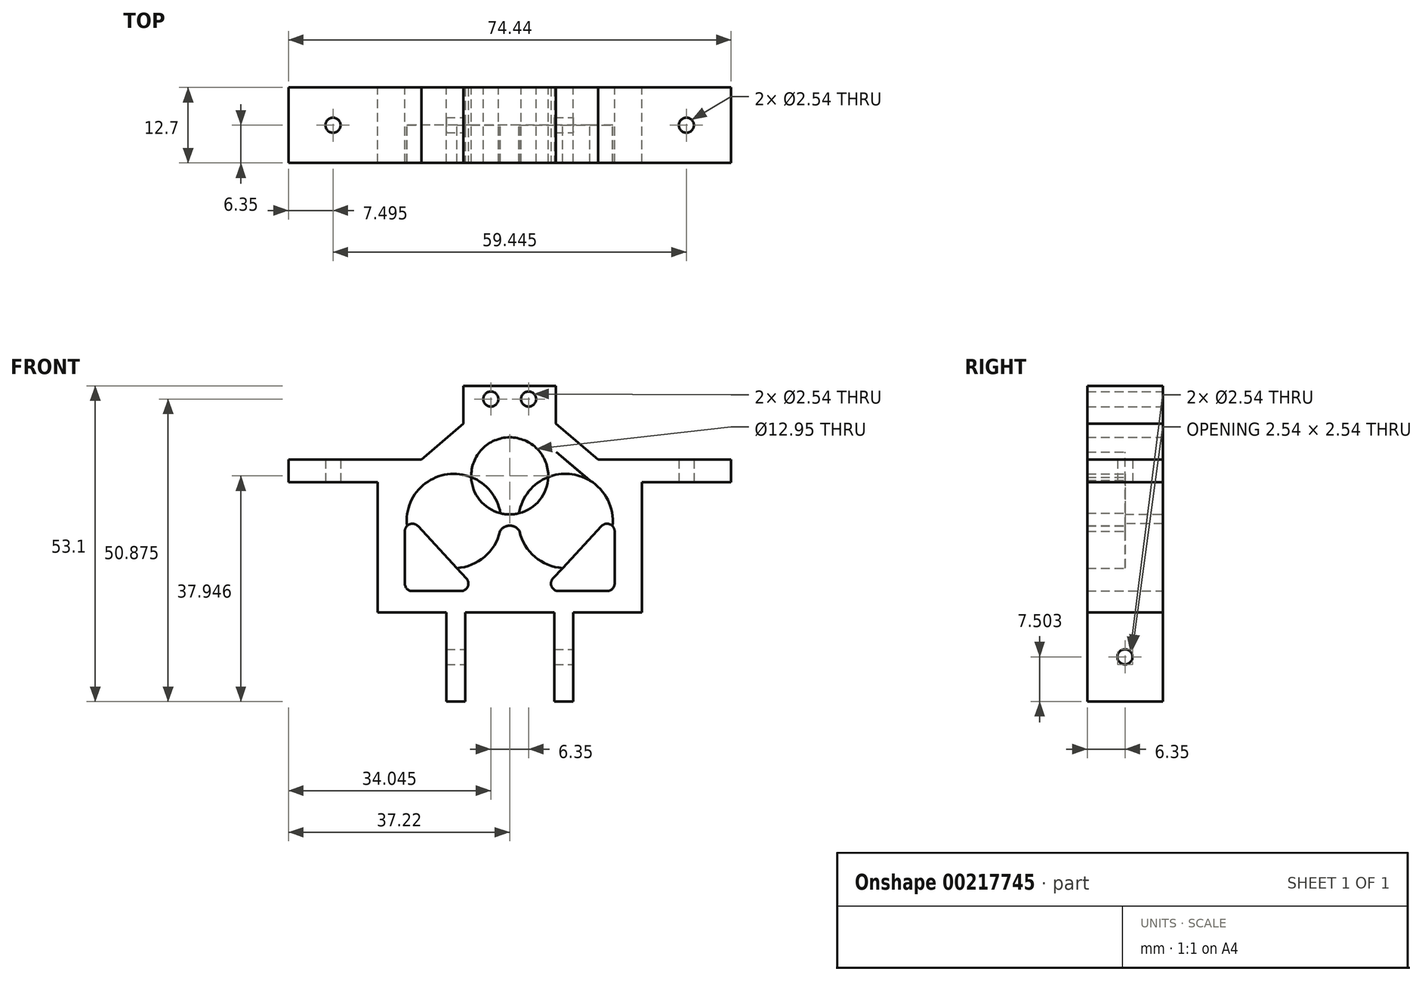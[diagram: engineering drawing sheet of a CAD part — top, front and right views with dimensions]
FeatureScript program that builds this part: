
annotation { "Feature Type Name" : "Feature", "Feature Type Description" : "" }
export const myFeature = defineFeature(function(context is Context, id is Id, definition is map)
    precondition{}
    {
        {
            var Q0;
            Q0=qCreatedBy(makeId("Front.planeOp"),FACE);
            var sketch = newSketch(context, id + "F0", { "sketchPlane" : qUnion([Q0])});
            skLineSegment(sketch, "E0", {"start": v(0, 0.13) * mm, "end": v(7.5, 0.13) * mm});
            skLineSegment(sketch, "E1", {"start": v(-22.22, 19.5) * mm, "end": v(-22.22, 4.52) * mm});
            skLineSegment(sketch, "E2", {"start": v(-7.5, 0.13) * mm, "end": v(0, 0.13) * mm});
            skArc(sketch, "E3", {"start": v(-13.47, 22.3) * mm, "mid": v(-14.04, 9.06) * mm, "end": v(-1.65, 13.77) * mm});
            skArc(sketch, "E4.MirrorC", {"start": v(13.47, 22.3) * mm, "mid": v(14.05, 9.06) * mm, "end": v(1.65, 13.75) * mm});
            skArc(sketch, "E5", {"start": v(1.65, 13.75) * mm, "mid": v(0, 14.71) * mm, "end": v(-1.65, 13.77) * mm});
            skLineSegment(sketch, "E6", {"start": v(-22.22, 19.5) * mm, "end": v(-22.22, 0.13) * mm});
            skLineSegment(sketch, "E7.MirrorCS", {"start": v(22.22, 19.5) * mm, "end": v(22.22, 0.13) * mm});
            skLineSegment(sketch, "E8", {"start": v(0, 0.13) * mm, "end": v(-22.22, 0.13) * mm});
            skLineSegment(sketch, "E9", {"start": v(0, 0.13) * mm, "end": v(22.22, 0.13) * mm});
            skPoint(sketch, "E10.orphan", {"position": v(-22.22, 0) * mm});
            skLineSegment(sketch, "E11", {"start": v(-3.18, 27.12) * mm, "end": v(-3.18, 30.3) * mm});
            skLineSegment(sketch, "E12", {"start": v(3.17, 30.3) * mm, "end": v(3.17, 27.12) * mm});
            skLineSegment(sketch, "E13", {"start": v(3.17, 27.12) * mm, "end": v(3.17, 27.12) * mm});
            skLineSegment(sketch, "E14", {"start": v(-22.22, 19.5) * mm, "end": v(-7.77, 31.88) * mm});
            skLineSegment(sketch, "E15", {"start": v(-3.18, 27.12) * mm, "end": v(-7.84, 27.12) * mm});
            skLineSegment(sketch, "E16", {"start": v(-13.47, 22.3) * mm, "end": v(-7.84, 27.12) * mm});
            skLineSegment(sketch, "E17.MirrorCS", {"start": v(3.17, 27.12) * mm, "end": v(7.84, 27.12) * mm});
            skLineSegment(sketch, "E18.MirrorCS", {"start": v(13.46, 22.3) * mm, "end": v(7.84, 27.12) * mm});
            skLineSegment(sketch, "E19.MirrorCS", {"start": v(3.17, 30.3) * mm, "end": v(3.18, 30.3) * mm});
            skLineSegment(sketch, "E20.MirrorCS", {"start": v(22.22, 19.5) * mm, "end": v(7.77, 31.88) * mm});
            skPoint(sketch, "E21.end.orphan", {"position": v(-9.63, 30.3) * mm});
            skPoint(sketch, "E22.orphan", {"position": v(9.62, 30.3) * mm});
            skPoint(sketch, "E23.start.orphan", {"position": v(0, 27.12) * mm});
            skLineSegment(sketch, "E24", {"start": v(13.47, 22.3) * mm, "end": v(7.84, 27.12) * mm});
            skLineSegment(sketch, "E25", {"start": v(3.17, 27.12) * mm, "end": v(3.17, 30.3) * mm});
            skLineSegment(sketch, "E26", {"start": v(-3.18, 30.3) * mm, "end": v(-3.18, 27.12) * mm});
            skLineSegment(sketch, "E27", {"start": v(-7.84, 27.12) * mm, "end": v(-13.47, 22.3) * mm});
            skArc(sketch, "E28", {"start": v(1.65, 13.75) * mm, "mid": v(14.06, 9.07) * mm, "end": v(13.45, 22.31) * mm});
            skPoint(sketch, "E29.startSnap0", {"position": v(0, 30.3) * mm});
            skPoint(sketch, "E30.orphan", {"position": v(22.22, 2.54) * mm});
            skLineSegment(sketch, "E31", {"start": v(3.17, 30.3) * mm, "end": v(3.17, 33.47) * mm});
            skLineSegment(sketch, "E32", {"start": v(3.17, 33.47) * mm, "end": v(-3.18, 33.47) * mm});
            skLineSegment(sketch, "E33", {"start": v(-3.18, 33.47) * mm, "end": v(-3.18, 30.3) * mm});
            skLineSegment(sketch, "E34", {"start": v(-7.77, 31.88) * mm, "end": v(-7.77, 38.23) * mm});
            skLineSegment(sketch, "E35", {"start": v(7.77, 31.88) * mm, "end": v(7.77, 38.23) * mm});
            skLineSegment(sketch, "E36", {"start": v(7.77, 38.23) * mm, "end": v(-7.77, 38.23) * mm});
            skCircle(sketch, "E37", {"center": v(-9.4, 15.5) * mm, "radius": 7.94 * mm});
            skCircle(sketch, "E38", {"center": v(9.4, 15.5) * mm, "radius": 7.94 * mm});
            skCircle(sketch, "E39", {"center": v(0, 23.08) * mm, "radius": 6.48 * mm});
            skLineSegment(sketch, "E40", {"start": v(-22.22, 0.13) * mm, "end": v(-22.22, 25.81) * mm});
            skLineSegment(sketch, "E41", {"start": v(-22.22, 25.81) * mm, "end": v(-17.42, 25.81) * mm});
            skLineSegment(sketch, "E42", {"start": v(-17.42, 25.81) * mm, "end": v(-12.1, 25.81) * mm});
            skLineSegment(sketch, "E43", {"start": v(0, 12.81) * mm, "end": v(0, 7.67) * mm});
            skLineSegment(sketch, "E44.MirrorCS", {"start": v(22.22, 0.13) * mm, "end": v(22.22, 25.81) * mm});
            skLineSegment(sketch, "E45.MirrorCS", {"start": v(22.22, 25.81) * mm, "end": v(17.42, 25.81) * mm});
            skLineSegment(sketch, "E46.MirrorCS", {"start": v(17.42, 25.81) * mm, "end": v(12.09, 25.81) * mm});
            skCircle(sketch, "E47", {"center": v(3.17, 36) * mm, "radius": 1.27 * mm});
            skCircle(sketch, "E48", {"center": v(-3.18, 36) * mm, "radius": 1.27 * mm});
            skSolve(sketch);
        }
        {
            var Q0;
            Q0=qSketchRegion(id+"F0",true);
            var Q1;
            {var subQ0=sQuery(id+"F0.wireOp",EDGE,"E38");var subQ1=makeQuery(id+"F0.imprint","INTERSECT",VERTEX,{"derivedFrom":[sQuery(id+"F0.wireOp",EDGE,"E24"),subQ0]});Q1=makeQuery(id+"F0.imprint","IMPRINT",FACE,{"disambiguationData":[TD([[makeQuery(id+"F0.imprint","IMPRINT",EDGE,{"disambiguationData":[TD([[subQ1,-1.0]])],"derivedFrom":subQ0}),1.0]])]});}
            var Q2;
            {var subQ0=sQuery(id+"F0.wireOp",EDGE,"E37");var subQ1=makeQuery(id+"F0.imprint","INTERSECT",VERTEX,{"derivedFrom":[sQuery(id+"F0.wireOp",EDGE,"E27"),subQ0]});Q2=makeQuery(id+"F0.imprint","IMPRINT",FACE,{"disambiguationData":[TD([[makeQuery(id+"F0.imprint","IMPRINT",EDGE,{"disambiguationData":[TD([[subQ1,-1.0]])],"derivedFrom":subQ0}),1.0]])]});}
            var Q3;
            Q3=makeQuery(id+"F0.imprint","IMPRINT",FACE,{"disambiguationData":[TD([[makeQuery(id+"F0.imprint","IMPRINT",EDGE,{"derivedFrom":sQuery(id+"F0.wireOp",EDGE,"E15")}),1.0]])]});
            var Q4;
            {var subQ4=sQuery(id+"F0.wireOp",EDGE,"E31");Q4=makeQuery(id+"F0.imprint","IMPRINT",FACE,{"disambiguationData":[TD([[makeQuery(id+"F0.imprint","IMPRINT",EDGE,{"derivedFrom":subQ4}),1.0]])]});}
            var Q5;
            {var subQ0=sQuery(id+"F0.wireOp",EDGE,"E18.MirrorCS");var subQ5=sQuery(id+"F0.wireOp",EDGE,"E38");var subQ6=makeQuery(id+"F0.imprint","INTERSECT",VERTEX,{"derivedFrom":[subQ0,subQ5]});Q5=makeQuery(id+"F0.imprint","IMPRINT",FACE,{"disambiguationData":[TD([[makeQuery(id+"F0.imprint","IMPRINT",EDGE,{"disambiguationData":[TD([[subQ6,-1.0]])],"derivedFrom":subQ5}),-1.0]])]});}
            var Q6;
            {var subQ0=sQuery(id+"F0.wireOp",EDGE,"E5");Q6=makeQuery(id+"F0.imprint","IMPRINT",FACE,{"disambiguationData":[TD([[makeQuery(id+"F0.imprint","IMPRINT",EDGE,{"derivedFrom":subQ0}),-1.0]])]});}
            extrude(context, id + "F1", {"entities" : qUnion([Q0, Q1, Q2, Q3, Q4, Q5, Q6]), "depth" : 6.35 * mm, "offsetDistance" : 25.4 * mm});
        }
        {
            var Q0;
            Q0=makeQuery(id+"F1.opExtrude","CAP_FACE",FACE,{"disambiguationData":[OSD([sQuery(id+"F0.wireOp",EDGE,"E6"),sQuery(id+"F0.wireOp",EDGE,"E7.MirrorCS"),sQuery(id+"F0.wireOp",EDGE,"E8"),sQuery(id+"F0.wireOp",EDGE,"E9"),sQuery(id+"F0.wireOp",EDGE,"E14"),sQuery(id+"F0.wireOp",EDGE,"E18.MirrorCS"),sQuery(id+"F0.wireOp",EDGE,"E20.MirrorCS"),sQuery(id+"F0.wireOp",EDGE,"E24"),sQuery(id+"F0.wireOp",EDGE,"E34"),sQuery(id+"F0.wireOp",EDGE,"E35"),sQuery(id+"F0.wireOp",EDGE,"E36"),sQuery(id+"F0.wireOp",EDGE,"E38"),sQuery(id+"F0.wireOp",EDGE,"E39")])],"isStart":true});
            var sketch = newSketch(context, id + "F2", { "sketchPlane" : qUnion([Q0])});
            skCircle(sketch, "E49", {"center": v(0, 23.08) * mm, "radius": 6.48 * mm});
            skLineSegment(sketch, "E50", {"start": v(-22.22, 0.13) * mm, "end": v(22.22, 0.13) * mm});
            skLineSegment(sketch, "E51", {"start": v(7.77, 31.88) * mm, "end": v(7.77, 31.88) * mm});
            skLineSegment(sketch, "E52", {"start": v(7.77, 31.88) * mm, "end": v(7.77, 38.23) * mm});
            skLineSegment(sketch, "E53", {"start": v(7.77, 38.23) * mm, "end": v(-7.77, 38.23) * mm});
            skLineSegment(sketch, "E54", {"start": v(-7.77, 38.23) * mm, "end": v(-7.77, 31.88) * mm});
            skLineSegment(sketch, "E55", {"start": v(-7.77, 31.88) * mm, "end": v(-7.77, 31.88) * mm});
            skLineSegment(sketch, "E56", {"start": v(22.22, 0.13) * mm, "end": v(22.22, 25.81) * mm});
            skLineSegment(sketch, "E57", {"start": v(-22.22, 0.13) * mm, "end": v(-22.22, 25.81) * mm});
            skLineSegment(sketch, "E58", {"start": v(-22.22, 25.81) * mm, "end": v(-14.86, 25.81) * mm});
            skLineSegment(sketch, "E59", {"start": v(-14.86, 25.81) * mm, "end": v(-7.77, 31.88) * mm});
            skLineSegment(sketch, "E60", {"start": v(22.22, 25.81) * mm, "end": v(14.86, 25.81) * mm});
            skLineSegment(sketch, "E61", {"start": v(14.86, 25.81) * mm, "end": v(7.77, 31.88) * mm});
            skCircle(sketch, "E62", {"center": v(-3.17, 36) * mm, "radius": 1.27 * mm});
            skCircle(sketch, "E63", {"center": v(3.18, 36) * mm, "radius": 1.27 * mm});
            skSolve(sketch);
        }
        {
            var Q0;
            Q0=qSketchRegion(id+"F2",true);
            extrude(context, id + "F3", {"entities" : qUnion([Q0]), "operationType" : NewBodyOperationType.ADD, "depth" : 6.35 * mm});
        }
        {
            var Q0;
            Q0=makeQuery(id+"F3.boolean.opBoolean","MERGE",FACE,{"derivedFrom":[makeQuery(id+"F1.opExtrude","SWEPT_FACE",FACE,{"disambiguationData":[OSD([sQuery(id+"F0.wireOp",EDGE,"E40")])]}),makeQuery(id+"F3.opExtrude","SWEPT_FACE",FACE,{"disambiguationData":[OSD([sQuery(id+"F2.wireOp",EDGE,"E56")])]})]});
            var sketch = newSketch(context, id + "F4", { "sketchPlane" : qUnion([Q0])});
            skLineSegment(sketch, "E64", {"start": v(6.35, 0.13) * mm, "end": v(6.35, 22) * mm});
            skLineSegment(sketch, "E65", {"start": v(6.35, 22) * mm, "end": v(-6.35, 22) * mm});
            skLineSegment(sketch, "E66", {"start": v(-6.35, 22) * mm, "end": v(-6.35, 25.81) * mm});
            skLineSegment(sketch, "E67", {"start": v(-6.35, 25.81) * mm, "end": v(6.35, 25.81) * mm});
            skLineSegment(sketch, "E68", {"start": v(6.35, 25.81) * mm, "end": v(6.35, 22) * mm});
            skSolve(sketch);
        }
        {
            var Q0;
            Q0=qSketchRegion(id+"F4",true);
            extrude(context, id + "F5", {"entities" : qUnion([Q0]), "operationType" : NewBodyOperationType.ADD, "depth" : 15 * mm});
        }
        {
            var Q0;
            Q0=makeQuery(id+"F5.opExtrude","SWEPT_FACE",FACE,{"disambiguationData":[OSD([sQuery(id+"F4.wireOp",EDGE,"E65")])]});
            var sketch = newSketch(context, id + "F6", { "sketchPlane" : qUnion([Q0])});
            skLineSegment(sketch, "E69", {"start": v(-37.22, -6.35) * mm, "end": v(-22.22, 6.35) * mm});
            skCircle(sketch, "E70", {"center": v(-29.72, 0) * mm, "radius": 1.27 * mm});
            skSolve(sketch);
        }
        {
            var Q0;
            Q0=qSketchRegion(id+"F6",true);
            extrude(context, id + "F7", {"entities" : qUnion([Q0]), "operationType" : NewBodyOperationType.REMOVE, "oppositeDirection" : true, "depth" : 25.4 * mm});
        }
        {
            var Q0;
            Q0=makeQuery(id+"F3.boolean.opBoolean","MERGE",FACE,{"derivedFrom":[makeQuery(id+"F1.opExtrude","SWEPT_FACE",FACE,{"disambiguationData":[OSD([sQuery(id+"F0.wireOp",EDGE,"E44.MirrorCS")])]}),makeQuery(id+"F3.opExtrude","SWEPT_FACE",FACE,{"disambiguationData":[OSD([sQuery(id+"F2.wireOp",EDGE,"E57")])]})]});
            var sketch = newSketch(context, id + "F8", { "sketchPlane" : qUnion([Q0])});
            skLineSegment(sketch, "E71", {"start": v(-6.35, 0.13) * mm, "end": v(-6.35, 25.81) * mm});
            skLineSegment(sketch, "E72", {"start": v(-6.35, 25.81) * mm, "end": v(6.35, 25.81) * mm});
            skLineSegment(sketch, "E73", {"start": v(6.35, 25.81) * mm, "end": v(6.35, 22) * mm});
            skLineSegment(sketch, "E74", {"start": v(6.35, 22) * mm, "end": v(-6.35, 22) * mm});
            skSolve(sketch);
        }
        {
            var Q0;
            Q0=qSketchRegion(id+"F8",true);
            extrude(context, id + "F9", {"entities" : qUnion([Q0]), "operationType" : NewBodyOperationType.ADD, "depth" : 15 * mm});
        }
        {
            var Q0;
            Q0=makeQuery(id+"F9.opExtrude","SWEPT_FACE",FACE,{"disambiguationData":[OSD([sQuery(id+"F8.wireOp",EDGE,"E74")])]});
            var sketch = newSketch(context, id + "F10", { "sketchPlane" : qUnion([Q0])});
            skLineSegment(sketch, "E75", {"start": v(37.22, 6.35) * mm, "end": v(22.22, -6.35) * mm});
            skCircle(sketch, "E76", {"center": v(29.72, 0) * mm, "radius": 1.27 * mm});
            skSolve(sketch);
        }
        {
            var Q0;
            Q0=qSketchRegion(id+"F10",true);
            extrude(context, id + "F11", {"entities" : qUnion([Q0]), "operationType" : NewBodyOperationType.REMOVE, "oppositeDirection" : true, "depth" : 25.4 * mm});
        }
        {
            var Q0;
            Q0=makeQuery(id+"F3.boolean.opBoolean","MERGE",FACE,{"derivedFrom":[makeQuery(id+"F1.opExtrude","SWEPT_FACE",FACE,{"disambiguationData":[OSD([sQuery(id+"F0.wireOp",EDGE,"E8"),sQuery(id+"F0.wireOp",EDGE,"E9")])]}),makeQuery(id+"F3.opExtrude","SWEPT_FACE",FACE,{"disambiguationData":[OSD([sQuery(id+"F2.wireOp",EDGE,"E50")])]})]});
            var sketch = newSketch(context, id + "F12", { "sketchPlane" : qUnion([Q0])});
            skLineSegment(sketch, "E77", {"start": v(0, -6.35) * mm, "end": v(7.5, -6.35) * mm});
            skLineSegment(sketch, "E78", {"start": v(0, -6.35) * mm, "end": v(-7.5, -6.35) * mm});
            skLineSegment(sketch, "E79", {"start": v(-7.5, -6.35) * mm, "end": v(-7.5, 6.35) * mm});
            skLineSegment(sketch, "E80", {"start": v(-7.5, 6.35) * mm, "end": v(-10.67, 6.35) * mm});
            skLineSegment(sketch, "E81", {"start": v(-10.67, 6.35) * mm, "end": v(-10.67, -6.35) * mm});
            skLineSegment(sketch, "E82", {"start": v(-10.67, -6.35) * mm, "end": v(-7.5, -6.35) * mm});
            skLineSegment(sketch, "E83", {"start": v(7.5, -6.35) * mm, "end": v(7.5, 6.35) * mm});
            skLineSegment(sketch, "E84", {"start": v(7.5, 6.35) * mm, "end": v(10.67, 6.35) * mm});
            skLineSegment(sketch, "E85", {"start": v(10.67, 6.35) * mm, "end": v(10.67, -6.35) * mm});
            skLineSegment(sketch, "E86", {"start": v(10.67, -6.35) * mm, "end": v(7.5, -6.35) * mm});
            skSolve(sketch);
        }
        {
            var Q0;
            Q0=qSketchRegion(id+"F12",true);
            extrude(context, id + "F13", {"entities" : qUnion([Q0]), "operationType" : NewBodyOperationType.ADD, "depth" : 15 * mm});
        }
        {
            var Q0;
            Q0=makeQuery(id+"F13.opExtrude","SWEPT_FACE",FACE,{"disambiguationData":[OSD([sQuery(id+"F12.wireOp",EDGE,"E85")])]});
            var sketch = newSketch(context, id + "F14", { "sketchPlane" : qUnion([Q0])});
            skLineSegment(sketch, "E87", {"start": v(-6.35, 0.13) * mm, "end": v(6.35, -14.87) * mm});
            skCircle(sketch, "E88", {"center": v(0, -7.37) * mm, "radius": 1.27 * mm});
            skSolve(sketch);
        }
        {
            var Q0;
            Q0=qSketchRegion(id+"F14",true);
            extrude(context, id + "F15", {"entities" : qUnion([Q0]), "operationType" : NewBodyOperationType.REMOVE, "oppositeDirection" : true, "depth" : 25.4 * mm});
        }
        {
            var Q0;
            Q0=makeQuery(id+"F13.boolean.opBoolean","MERGE",FACE,{"derivedFrom":[makeQuery(id+"F9.boolean.opBoolean","MERGE",FACE,{"derivedFrom":[makeQuery(id+"F5.boolean.opBoolean","MERGE",FACE,{"derivedFrom":[makeQuery(id+"F3.opExtrude","CAP_FACE",FACE,{"disambiguationData":[OSD([sQuery(id+"F2.wireOp",EDGE,"E49"),sQuery(id+"F2.wireOp",EDGE,"E50"),sQuery(id+"F2.wireOp",EDGE,"E52"),sQuery(id+"F2.wireOp",EDGE,"E53"),sQuery(id+"F2.wireOp",EDGE,"E54"),sQuery(id+"F2.wireOp",EDGE,"E56"),sQuery(id+"F2.wireOp",EDGE,"E57"),sQuery(id+"F2.wireOp",EDGE,"E58"),sQuery(id+"F2.wireOp",EDGE,"E59"),sQuery(id+"F2.wireOp",EDGE,"E60"),sQuery(id+"F2.wireOp",EDGE,"E61"),sQuery(id+"F2.wireOp",EDGE,"E62"),sQuery(id+"F2.wireOp",EDGE,"E63")])],"isStart":false}),makeQuery(id+"F5.opExtrude","SWEPT_FACE",FACE,{"disambiguationData":[OSD([sQuery(id+"F4.wireOp",EDGE,"E66")])]})]}),makeQuery(id+"F9.opExtrude","SWEPT_FACE",FACE,{"disambiguationData":[OSD([sQuery(id+"F8.wireOp",EDGE,"E73")])]})]}),makeQuery(id+"F13.opExtrude","SWEPT_FACE",FACE,{"disambiguationData":[OSD([sQuery(id+"F12.wireOp",EDGE,"E82")])]}),makeQuery(id+"F13.opExtrude","SWEPT_FACE",FACE,{"disambiguationData":[OSD([sQuery(id+"F12.wireOp",EDGE,"E86")])]})]});
            var sketch = newSketch(context, id + "F16", { "sketchPlane" : qUnion([Q0])});
            skLineSegment(sketch, "E89", {"start": v(-17.64, 17) * mm, "end": v(-17.64, 3.7) * mm});
            skLineSegment(sketch, "E90", {"start": v(-17.64, 3.7) * mm, "end": v(-5.3, 3.7) * mm});
            skLineSegment(sketch, "E91", {"start": v(-5.3, 3.7) * mm, "end": v(-17.64, 17) * mm});
            skLineSegment(sketch, "E92", {"start": v(0, 0) * mm, "end": v(0, 10.22) * mm});
            skLineSegment(sketch, "E93.MirrorCS", {"start": v(5.3, 3.7) * mm, "end": v(17.64, 17) * mm});
            skLineSegment(sketch, "E94.MirrorCS", {"start": v(17.64, 17) * mm, "end": v(17.64, 3.7) * mm});
            skLineSegment(sketch, "E95.MirrorCS", {"start": v(17.64, 3.7) * mm, "end": v(5.3, 3.7) * mm});
            skSolve(sketch);
        }
        {
            var Q0;
            Q0 = qSketchRegion(id + "F16", true);
            extrude(context, id + "F17", {"entities" : qUnion([Q0]), "operationType" : NewBodyOperationType.REMOVE, "oppositeDirection" : true, "depth" : 25.4 * mm, "offsetDistance" : 25.4 * mm});
        }
        {
            var Q0;
            Q0=makeQuery(id+"F17.boolean.opBoolean","COPY",EDGE,{"derivedFrom":makeQuery(id+"F17.opExtrude","SWEPT_EDGE",EDGE,{"disambiguationData":[OSD([sQuery(id+"F16.wireOp",EDGE,"E89"),sQuery(id+"F16.wireOp",EDGE,"E91")])]})});
            var Q1;
            Q1=makeQuery(id+"F17.boolean.opBoolean","COPY",EDGE,{"derivedFrom":makeQuery(id+"F17.opExtrude","SWEPT_EDGE",EDGE,{"disambiguationData":[OSD([sQuery(id+"F16.wireOp",EDGE,"E90"),sQuery(id+"F16.wireOp",EDGE,"E91")])]})});
            var Q2;
            Q2=makeQuery(id+"F17.boolean.opBoolean","COPY",EDGE,{"derivedFrom":makeQuery(id+"F17.opExtrude","SWEPT_EDGE",EDGE,{"disambiguationData":[OSD([sQuery(id+"F16.wireOp",EDGE,"E89"),sQuery(id+"F16.wireOp",EDGE,"E90")])]})});
            var Q3;
            Q3=makeQuery(id+"F17.boolean.opBoolean","COPY",EDGE,{"derivedFrom":makeQuery(id+"F17.opExtrude","SWEPT_EDGE",EDGE,{"disambiguationData":[OSD([sQuery(id+"F16.wireOp",EDGE,"E93.MirrorCS"),sQuery(id+"F16.wireOp",EDGE,"E95.MirrorCS")])]})});
            var Q4;
            Q4=makeQuery(id+"F17.boolean.opBoolean","COPY",EDGE,{"derivedFrom":makeQuery(id+"F17.opExtrude","SWEPT_EDGE",EDGE,{"disambiguationData":[OSD([sQuery(id+"F16.wireOp",EDGE,"E93.MirrorCS"),sQuery(id+"F16.wireOp",EDGE,"E94.MirrorCS")])]})});
            var Q5;
            Q5=makeQuery(id+"F17.boolean.opBoolean","COPY",EDGE,{"derivedFrom":makeQuery(id+"F17.opExtrude","SWEPT_EDGE",EDGE,{"disambiguationData":[OSD([sQuery(id+"F16.wireOp",EDGE,"E94.MirrorCS"),sQuery(id+"F16.wireOp",EDGE,"E95.MirrorCS")])]})});
            fillet(context, id + "F18", {"entities" : qUnion([Q0, Q1, Q2, Q3, Q4, Q5]), "radius" : 1.27 * mm, "tangentPropagation" : true, "allowEdgeOverflow" : false});
        }
    });
